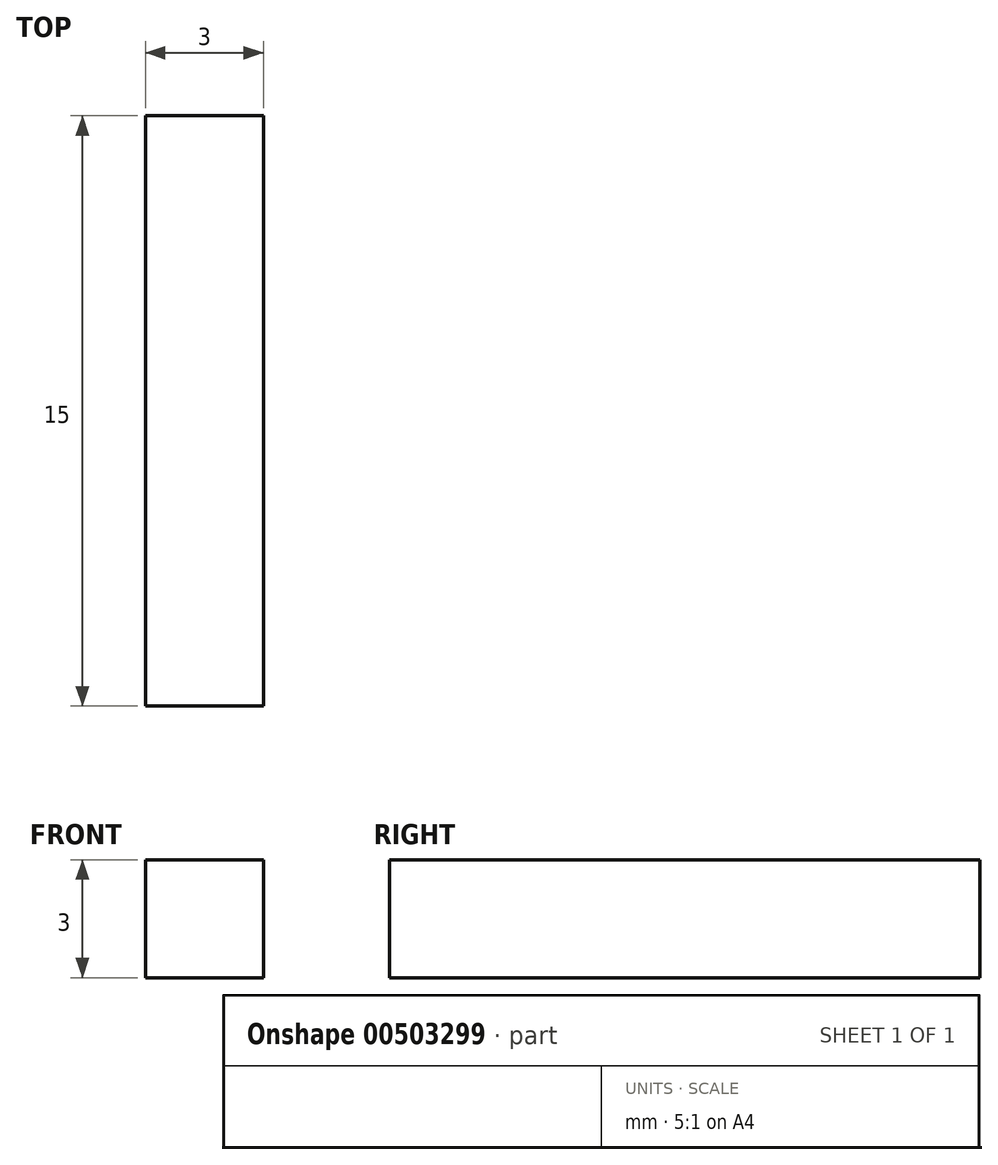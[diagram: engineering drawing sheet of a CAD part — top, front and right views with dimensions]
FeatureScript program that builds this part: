
annotation { "Feature Type Name" : "Feature", "Feature Type Description" : "" }
export const myFeature = defineFeature(function(context is Context, id is Id, definition is map)
    precondition{}
    {
        {
            var Q0;
            Q0=qCreatedBy(makeId("Top.planeOp"),FACE);
            var sketch = newSketch(context, id + "F0", { "sketchPlane" : qUnion([Q0])});
            skLineSegment(sketch, "E0.bottom", {"start": v(0, 0) * mm, "end": v(-3, 0) * mm});
            skLineSegment(sketch, "E0.top", {"start": v(0, 15) * mm, "end": v(-3, 15) * mm});
            skLineSegment(sketch, "E0.left", {"start": v(0, 0) * mm, "end": v(0, 15) * mm});
            skLineSegment(sketch, "E0.right", {"start": v(-3, 0) * mm, "end": v(-3, 15) * mm});
            skSolve(sketch);
        }
        {
            var Q0;
            Q0=makeQuery(id+"F0.imprint","IMPRINT",FACE,{"disambiguationData":[TD([[makeQuery(id+"F0.imprint","IMPRINT",EDGE,{"derivedFrom":sQuery(id+"F0.wireOp",EDGE,"E0.bottom")}),-1.0]])]});
            extrude(context, id + "F1", {"entities" : qUnion([Q0]), "depth" : 3 * mm});
        }
    });
